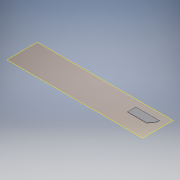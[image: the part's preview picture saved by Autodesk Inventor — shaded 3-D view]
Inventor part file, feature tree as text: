
AUTODESK INVENTOR PART (.ipt)
format: ipt  version: 2018 (Build 220112000, 112)  size: 110,080 bytes
history: native  units: mm
features: other x4, plane x1, sheet_metal_op x1, sketch x1
ambient origin geometry x8: Origin, YZ Plane, XZ Plane, XY Plane, X Axis, Y Axis, Z Axis, Center Point
bodies: Solid1 (feature_tree)
feature tree (7):
  plane  "Work Plane1"
  sheet_metal_op  "Face1"
  sketch  "Sketch1"  dims[d0=9.721484mm d1=2.0mm d2=200.0mm d3=20.0mm d4=226.0mm]
  other  "Plate1"
  parser-record x1  (decoder bookkeeping rows leaked as tree rows — omitted from the tree; the rows remain in map.json)
  other  "svejselære.iam"
  other  "plade:1"
note: 1 file-system path scrubbed to <path> (originals preserved in map.json)
